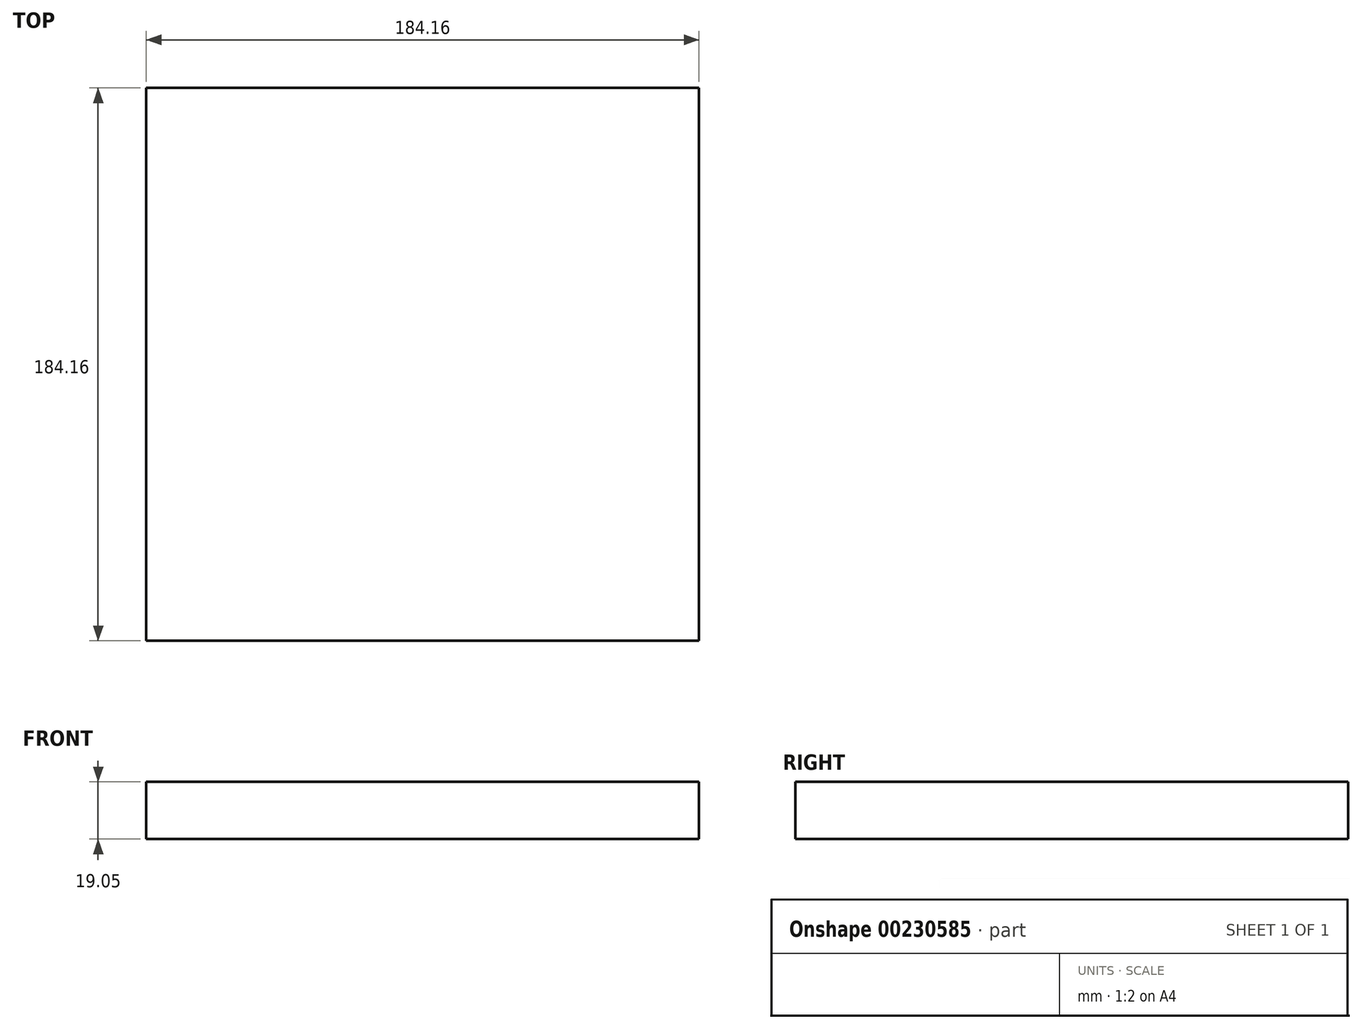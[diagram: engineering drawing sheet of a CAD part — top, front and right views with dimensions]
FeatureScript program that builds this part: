
annotation { "Feature Type Name" : "Feature", "Feature Type Description" : "" }
export const myFeature = defineFeature(function(context is Context, id is Id, definition is map)
    precondition{}
    {
        {
            var Q0;
            Q0=qCreatedBy(makeId("Top.planeOp"),FACE);
            var sketch = newSketch(context, id + "F0", { "sketchPlane" : qUnion([Q0])});
            skLineSegment(sketch, "E0.bottom", {"start": v(92.08, -92.07) * mm, "end": v(-92.08, -92.08) * mm});
            skLineSegment(sketch, "E0.top", {"start": v(92.08, 92.08) * mm, "end": v(-92.07, 92.07) * mm});
            skLineSegment(sketch, "E0.left", {"start": v(92.08, -92.07) * mm, "end": v(92.08, 92.07) * mm});
            skLineSegment(sketch, "E0.right", {"start": v(-92.08, -92.08) * mm, "end": v(-92.07, 92.07) * mm});
            skPoint(sketch, "E0.middle", {"position": v(0, 0) * mm});
            skSolve(sketch);
        }
        {
            var Q0;
            Q0=makeQuery(id+"F0.imprint","IMPRINT",FACE,{"disambiguationData":[TD([[makeQuery(id+"F0.imprint","IMPRINT",EDGE,{"derivedFrom":sQuery(id+"F0.wireOp",EDGE,"E0.bottom")}),-1.0]])]});
            extrude(context, id + "F1", {"entities" : qUnion([Q0]), "depth" : 19.05 * mm});
        }
    });
